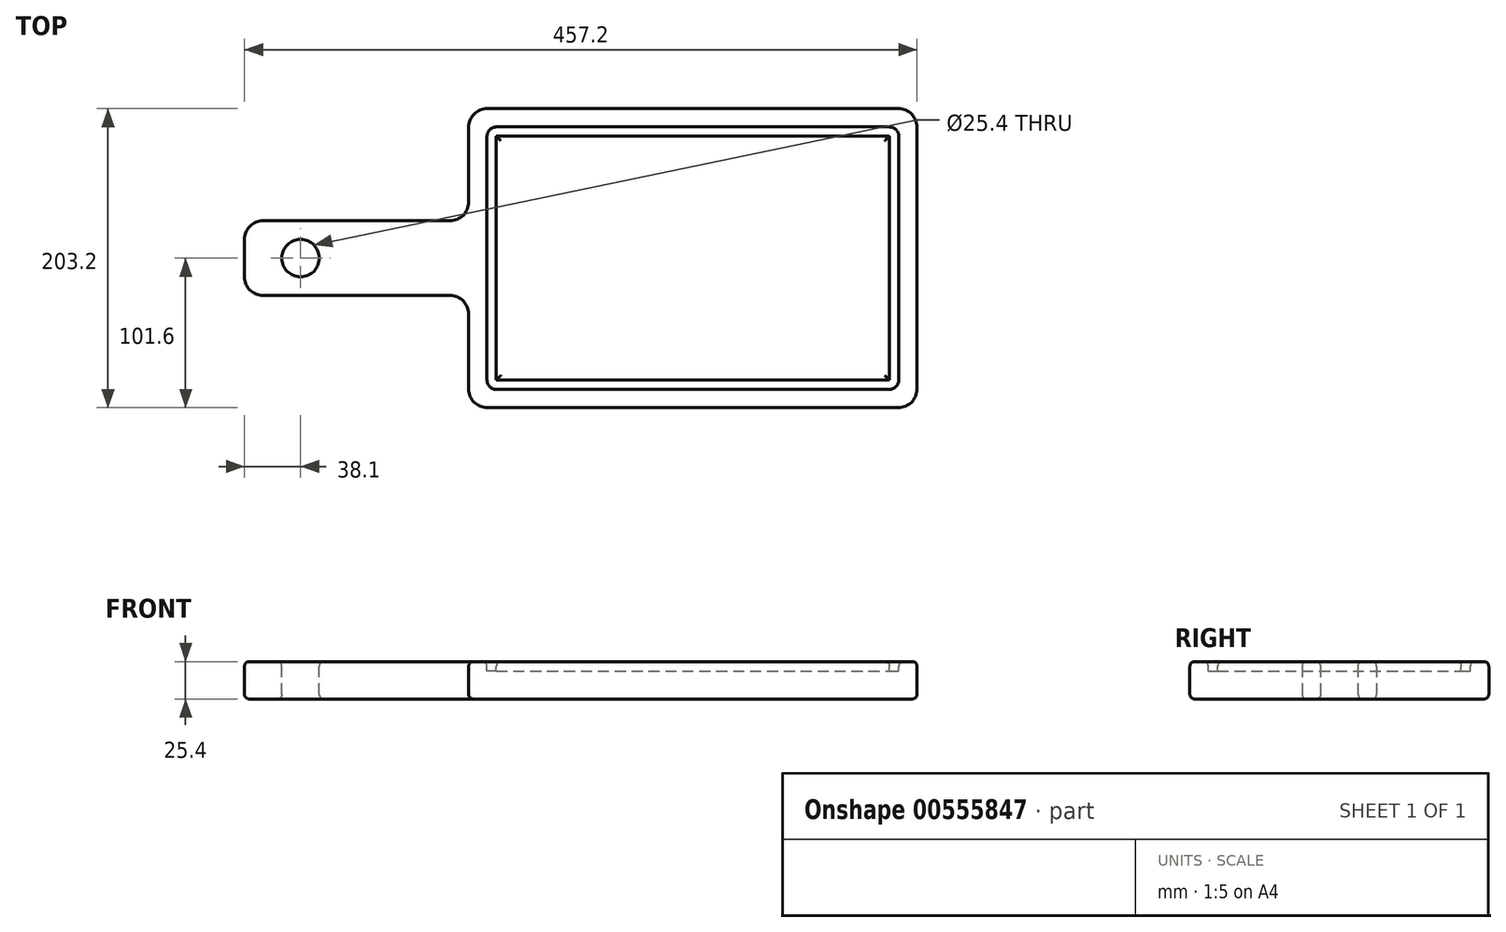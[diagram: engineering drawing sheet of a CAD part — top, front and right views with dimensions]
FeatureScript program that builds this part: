
annotation { "Feature Type Name" : "Feature", "Feature Type Description" : "" }
export const myFeature = defineFeature(function(context is Context, id is Id, definition is map)
    precondition{}
    {
        {
            var Q0;
            Q0=qCreatedBy(makeId("Top.planeOp"),FACE);
            var sketch = newSketch(context, id + "F0", { "sketchPlane" : qUnion([Q0])});
            skLineSegment(sketch, "E0.bottom", {"start": v(0, 0) * mm, "end": v(304.8, 0) * mm});
            skLineSegment(sketch, "E0.top", {"start": v(0, 203.2) * mm, "end": v(304.8, 203.2) * mm});
            skLineSegment(sketch, "E0.left", {"start": v(0, 0) * mm, "end": v(0, 203.2) * mm});
            skLineSegment(sketch, "E0.right", {"start": v(304.8, 0) * mm, "end": v(304.8, 203.2) * mm});
            skLineSegment(sketch, "E1.bottom", {"start": v(0, 76.2) * mm, "end": v(-152.4, 76.2) * mm});
            skLineSegment(sketch, "E1.top", {"start": v(0, 127) * mm, "end": v(-152.4, 127) * mm});
            skLineSegment(sketch, "E1.left", {"start": v(0, 76.2) * mm, "end": v(0, 127) * mm});
            skLineSegment(sketch, "E1.right", {"start": v(-152.4, 76.2) * mm, "end": v(-152.4, 127) * mm});
            skSolve(sketch);
        }
        {
            var Q0;
            {var subQ3=sQuery(id+"F0.wireOp",EDGE,"E0.bottom");Q0=makeQuery(id+"F0.imprint","IMPRINT",FACE,{"disambiguationData":[TD([[makeQuery(id+"F0.imprint","IMPRINT",EDGE,{"derivedFrom":subQ3}),1.0]])]});}
            var Q1;
            Q1=makeQuery(id+"F0.imprint","IMPRINT",FACE,{"disambiguationData":[TD([[makeQuery(id+"F0.imprint","IMPRINT",EDGE,{"derivedFrom":sQuery(id+"F0.wireOp",EDGE,"E1.bottom")}),-1.0]])]});
            extrude(context, id + "F1", {"entities" : qUnion([Q0, Q1]), "depth" : 25.4 * mm, "offsetDistance" : 25.4 * mm});
        }
        {
            var Q0;
            Q0=makeQuery(id+"F1.opExtrude","CAP_FACE",FACE,{"disambiguationData":[OSD([sQuery(id+"F0.wireOp",EDGE,"E0.bottom"),sQuery(id+"F0.wireOp",EDGE,"E0.top"),sQuery(id+"F0.wireOp",EDGE,"E0.left"),sQuery(id+"F0.wireOp",EDGE,"E0.right"),sQuery(id+"F0.wireOp",EDGE,"E1.bottom"),sQuery(id+"F0.wireOp",EDGE,"E1.top"),sQuery(id+"F0.wireOp",EDGE,"E1.right")])],"isStart":false});
            var sketch = newSketch(context, id + "F2", { "sketchPlane" : qUnion([Q0])});
            skCircle(sketch, "E2", {"center": v(-114.3, 101.6) * mm, "radius": 12.7 * mm});
            skSolve(sketch);
        }
        {
            var Q0;
            Q0=makeQuery(id+"F2.imprint","IMPRINT",FACE,{"disambiguationData":[TD([[makeQuery(id+"F2.imprint","IMPRINT",EDGE,{"derivedFrom":sQuery(id+"F2.wireOp",EDGE,"E2")}),1.0]])]});
            extrude(context, id + "F3", {"entities" : qUnion([Q0]), "operationType" : NewBodyOperationType.REMOVE, "oppositeDirection" : true, "depth" : 25.4 * mm, "offsetDistance" : 25.4 * mm});
        }
        {
            var Q0;
            Q0=makeQuery(id+"F1.opExtrude","CAP_FACE",FACE,{"disambiguationData":[OSD([sQuery(id+"F0.wireOp",EDGE,"E0.bottom"),sQuery(id+"F0.wireOp",EDGE,"E0.top"),sQuery(id+"F0.wireOp",EDGE,"E0.left"),sQuery(id+"F0.wireOp",EDGE,"E0.right"),sQuery(id+"F0.wireOp",EDGE,"E1.bottom"),sQuery(id+"F0.wireOp",EDGE,"E1.top"),sQuery(id+"F0.wireOp",EDGE,"E1.right")])],"isStart":false});
            var sketch = newSketch(context, id + "F4", { "sketchPlane" : qUnion([Q0])});
            skLineSegment(sketch, "E3.0", {"start": v(12.45, 12.45) * mm, "end": v(12.45, 76.2) * mm});
            skLineSegment(sketch, "E3.1", {"start": v(12.45, 76.2) * mm, "end": v(12.45, 190.75) * mm});
            skLineSegment(sketch, "E3.2", {"start": v(12.45, 190.75) * mm, "end": v(292.35, 190.75) * mm});
            skLineSegment(sketch, "E3.3", {"start": v(292.35, 12.45) * mm, "end": v(292.35, 190.75) * mm});
            skLineSegment(sketch, "E3.4", {"start": v(12.45, 12.45) * mm, "end": v(292.35, 12.45) * mm});
            skLineSegment(sketch, "E4.0", {"start": v(286, 18.8) * mm, "end": v(286, 184.4) * mm});
            skLineSegment(sketch, "E4.1", {"start": v(18.8, 184.4) * mm, "end": v(286, 184.4) * mm});
            skLineSegment(sketch, "E4.2", {"start": v(18.8, 18.8) * mm, "end": v(286, 18.8) * mm});
            skLineSegment(sketch, "E4.3", {"start": v(18.8, 18.8) * mm, "end": v(18.8, 76.2) * mm});
            skLineSegment(sketch, "E4.4", {"start": v(18.8, 76.2) * mm, "end": v(18.8, 184.4) * mm});
            skSolve(sketch);
        }
        {
            var Q0;
            Q0=makeQuery(id+"F4.imprint","IMPRINT",FACE,{"disambiguationData":[TD([[makeQuery(id+"F4.imprint","IMPRINT",EDGE,{"derivedFrom":sQuery(id+"F4.wireOp",EDGE,"E3.0")}),-1.0]])]});
            extrude(context, id + "F5", {"entities" : qUnion([Q0]), "operationType" : NewBodyOperationType.REMOVE, "oppositeDirection" : true, "depth" : 6.35 * mm, "offsetDistance" : 25.4 * mm});
        }
        {
            var Q0;
            Q0=makeQuery(id+"F5.boolean.opBoolean","COPY",EDGE,{"derivedFrom":makeQuery(id+"F5.opExtrude","SWEPT_EDGE",EDGE,{"disambiguationData":[OSD([sQuery(id+"F4.wireOp",EDGE,"E3.1"),sQuery(id+"F4.wireOp",EDGE,"E3.2")])]})});
            var Q1;
            Q1=makeQuery(id+"F5.boolean.opBoolean","COPY",EDGE,{"derivedFrom":makeQuery(id+"F5.opExtrude","SWEPT_EDGE",EDGE,{"disambiguationData":[OSD([sQuery(id+"F4.wireOp",EDGE,"E3.2"),sQuery(id+"F4.wireOp",EDGE,"E3.3")])]})});
            var Q2;
            Q2=makeQuery(id+"F5.boolean.opBoolean","COPY",EDGE,{"derivedFrom":makeQuery(id+"F5.opExtrude","SWEPT_EDGE",EDGE,{"disambiguationData":[OSD([sQuery(id+"F4.wireOp",EDGE,"E3.0"),sQuery(id+"F4.wireOp",EDGE,"E3.4")])]})});
            fillet(context, id + "F6", {"entities" : qUnion([Q0, Q1, Q2]), "radius" : 6.35 * mm, "tangentPropagation" : true, "allowEdgeOverflow" : false});
        }
        {
            var Q0;
            Q0=makeQuery(id+"F5.boolean.opBoolean","COPY",EDGE,{"derivedFrom":makeQuery(id+"F5.opExtrude","SWEPT_EDGE",EDGE,{"disambiguationData":[OSD([sQuery(id+"F4.wireOp",EDGE,"E3.3"),sQuery(id+"F4.wireOp",EDGE,"E3.4")])]})});
            fillet(context, id + "F7", {"entities" : qUnion([Q0]), "radius" : 6.35 * mm, "tangentPropagation" : true, "allowEdgeOverflow" : false});
        }
        {
            var Q0;
            Q0=makeQuery(id+"F1.opExtrude","SWEPT_EDGE",EDGE,{"disambiguationData":[OSD([sQuery(id+"F0.wireOp",EDGE,"E0.top"),sQuery(id+"F0.wireOp",EDGE,"E0.left")])]});
            var Q1;
            Q1=makeQuery(id+"F1.opExtrude","SWEPT_EDGE",EDGE,{"disambiguationData":[OSD([sQuery(id+"F0.wireOp",EDGE,"E1.top"),sQuery(id+"F0.wireOp",EDGE,"E1.right")])]});
            var Q2;
            Q2=makeQuery(id+"F1.opExtrude","SWEPT_EDGE",EDGE,{"disambiguationData":[OSD([sQuery(id+"F0.wireOp",EDGE,"E1.bottom"),sQuery(id+"F0.wireOp",EDGE,"E1.right")])]});
            var Q3;
            Q3=makeQuery(id+"F1.opExtrude","SWEPT_EDGE",EDGE,{"disambiguationData":[OSD([sQuery(id+"F0.wireOp",EDGE,"E0.bottom"),sQuery(id+"F0.wireOp",EDGE,"E0.left")])]});
            var Q4;
            Q4=makeQuery(id+"F1.opExtrude","SWEPT_EDGE",EDGE,{"disambiguationData":[OSD([sQuery(id+"F0.wireOp",EDGE,"E0.top"),sQuery(id+"F0.wireOp",EDGE,"E0.right")])]});
            var Q5;
            Q5=makeQuery(id+"F1.opExtrude","SWEPT_EDGE",EDGE,{"disambiguationData":[OSD([sQuery(id+"F0.wireOp",EDGE,"E0.bottom"),sQuery(id+"F0.wireOp",EDGE,"E0.right")])]});
            var Q6;
            Q6=makeQuery(id+"F1.opExtrude","SWEPT_EDGE",EDGE,{"disambiguationData":[OSD([sQuery(id+"F0.wireOp",EDGE,"E0.left"),sQuery(id+"F0.wireOp",EDGE,"E1.bottom"),sQuery(id+"F0.wireOp",EDGE,"E1.left")])]});
            var Q7;
            Q7=makeQuery(id+"F1.opExtrude","SWEPT_EDGE",EDGE,{"disambiguationData":[OSD([sQuery(id+"F0.wireOp",EDGE,"E0.left"),sQuery(id+"F0.wireOp",EDGE,"E1.top"),sQuery(id+"F0.wireOp",EDGE,"E1.left")])]});
            fillet(context, id + "F8", {"entities" : qUnion([Q0, Q1, Q2, Q3, Q4, Q5, Q6, Q7]), "radius" : 12.7 * mm, "tangentPropagation" : true, "allowEdgeOverflow" : false});
        }
        {
            var Q0;
            Q0=makeQuery(id+"F5.boolean.opBoolean","SPLIT",FACE,{"disambiguationData":[TD([makeQuery(id+"F5.opExtrude","SWEPT_FACE",FACE,{"disambiguationData":[OSD([sQuery(id+"F4.wireOp",EDGE,"E4.0")])]})])],"derivedFrom":makeQuery(id+"F1.opExtrude","CAP_FACE",FACE,{"disambiguationData":[OSD([sQuery(id+"F0.wireOp",EDGE,"E0.bottom"),sQuery(id+"F0.wireOp",EDGE,"E0.top"),sQuery(id+"F0.wireOp",EDGE,"E0.left"),sQuery(id+"F0.wireOp",EDGE,"E0.right"),sQuery(id+"F0.wireOp",EDGE,"E1.bottom"),sQuery(id+"F0.wireOp",EDGE,"E1.top"),sQuery(id+"F0.wireOp",EDGE,"E1.right")])],"isStart":false})});
            var Q1;
            {var subQ0=sQuery(id+"F0.wireOp",EDGE,"E1.right");var subQ1=sQuery(id+"F0.wireOp",EDGE,"E1.top");var subQ2=sQuery(id+"F0.wireOp",EDGE,"E1.bottom");var subQ3=sQuery(id+"F0.wireOp",EDGE,"E0.right");var subQ4=sQuery(id+"F0.wireOp",EDGE,"E0.bottom");var subQ5=sQuery(id+"F0.wireOp",EDGE,"E0.left");var subQ6=sQuery(id+"F0.wireOp",EDGE,"E0.top");Q1=makeQuery(id+"F5.boolean.opBoolean","SPLIT",FACE,{"disambiguationData":[TD([makeQuery(id+"F1.opExtrude","SWEPT_FACE",FACE,{"disambiguationData":[OSD([subQ4])]})])],"derivedFrom":makeQuery(id+"F1.opExtrude","CAP_FACE",FACE,{"disambiguationData":[OSD([subQ4,subQ6,subQ5,subQ3,subQ2,subQ1,subQ0])],"isStart":false})});}
            var Q2;
            Q2=makeQuery(id+"F1.opExtrude","CAP_FACE",FACE,{"disambiguationData":[OSD([sQuery(id+"F0.wireOp",EDGE,"E0.bottom"),sQuery(id+"F0.wireOp",EDGE,"E0.top"),sQuery(id+"F0.wireOp",EDGE,"E0.left"),sQuery(id+"F0.wireOp",EDGE,"E0.right"),sQuery(id+"F0.wireOp",EDGE,"E1.bottom"),sQuery(id+"F0.wireOp",EDGE,"E1.top"),sQuery(id+"F0.wireOp",EDGE,"E1.right")])],"isStart":true});
            fillet(context, id + "F9", {"entities" : qUnion([Q0, Q1, Q2]), "radius" : 3.17 * mm, "tangentPropagation" : true, "allowEdgeOverflow" : false});
        }
    });
